# Revit family: QF_BOURGEAT_Self_Meuble_buffet_cuve_froid_statique
name_source: partatom
category: Modèles génériques
revit_build: Autodesk Revit 2015 (Build: 20140606_1530(x64)
units: mm (PartAtom-declared; Revit-internal decimal feet)

## types (12) — shared parameters
Charge max = 200.00 kg
Classe Climatique = 3
Fabricant = BOURGEAT
Fréquence = 50 Hz
Indice de protection = 21
Intensité nominale = 1 A
Nature isolant = mousse polyurethane
Niveau Sonore = 60dBa
Phase = 2
Profondeur hors tout = 1465 mm  [stored 4.80643 ft]
Puissance frigorifique = 272W
Spécification du Fabricant = Meuble buffet cuve froid statique OASIS
Tension = 230 V
Type Fluide Frigorigène = R404a
URL catalogue = http://www.bourgeat.fr

## per-type parameters (varying)
| type | Hauteur hors tout | Longueur hors tout | Modèle | Poids net à vide | Puissance électrique  | lg_barre | lg_meuble_et_cuve | lg_presentoir | pieds | presentoir | roues |
| 5GN-buffet | 900 mm  [stored 2.95276 ft] | 2383 mm  [stored 7.81824 ft] | 853595 | 250.00 kg | 300 W | 1807 mm  [stored 5.92848 ft] | 1851 mm  [stored 6.07283 ft] | 1739 mm  [stored 5.70538 ft] | Oui | Non | Non |
| 5GN-buffet+presentoir_lampe_fluorecente | 1330 mm  [stored 4.36352 ft] | 2383 mm  [stored 7.81824 ft] | 853595+853335 | 277.00 kg | 340 W | 1807 mm  [stored 5.92848 ft] | 1851 mm  [stored 6.07283 ft] | 1739 mm  [stored 5.70538 ft] | Oui | Oui | Non |
| 5GN-buffet+presentoir_lampe_LED | 1330 mm  [stored 4.36352 ft] | 2383 mm  [stored 7.81824 ft] | 853595+853345 | 277.00 kg | 340 W | 1807 mm  [stored 5.92848 ft] | 1851 mm  [stored 6.07283 ft] | 1739 mm  [stored 5.70538 ft] | Oui | Oui | Non |
| 5GN-buffet+roues | 900 mm  [stored 2.95276 ft] | 2383 mm  [stored 7.81824 ft] | 853595+854950 | 250.00 kg | 300 W | 1807 mm  [stored 5.92848 ft] | 1851 mm  [stored 6.07283 ft] | 1739 mm  [stored 5.70538 ft] | Non | Non | Oui |
| 5GN-buffet+presentoir_lampe_fluorecente+roues | 1330 mm  [stored 4.36352 ft] | 2383 mm  [stored 7.81824 ft] | 853595+853335+854950 | 277.00 kg | 340 W | 1807 mm  [stored 5.92848 ft] | 1851 mm  [stored 6.07283 ft] | 1739 mm  [stored 5.70538 ft] | Non | Oui | Oui |
| 5GN-buffet+presentoir_lampe_LED+roues | 1330 mm  [stored 4.36352 ft] | 2383 mm  [stored 7.81824 ft] | 853595+853345+854950 | 277.00 kg | 340 W | 1807 mm  [stored 5.92848 ft] | 1851 mm  [stored 6.07283 ft] | 1739 mm  [stored 5.70538 ft] | Non | Oui | Oui |
| 4GN-buffet | 900 mm  [stored 2.95276 ft] | 2066 mm  [stored 6.77822 ft] | 853594 | 220.00 kg | 300 W | 1490 mm  [stored 4.88845 ft] | 1534 mm  [stored 5.03281 ft] | 1422 mm  [stored 4.66535 ft] | Oui | Non | Non |
| 4GN-buffet+presentoir_lampe_fluorecente | 900 mm  [stored 2.95276 ft] | 2066 mm  [stored 6.77822 ft] | 853594+853334 | 242.00 kg | 332 W | 1490 mm  [stored 4.88845 ft] | 1534 mm  [stored 5.03281 ft] | 1422 mm  [stored 4.66535 ft] | Oui | Oui | Non |
| 4GN-buffet+presentoir_lampe_LED | 900 mm  [stored 2.95276 ft] | 2066 mm  [stored 6.77822 ft] | 853594+853344 | 242.00 kg | 332 W | 1490 mm  [stored 4.88845 ft] | 1534 mm  [stored 5.03281 ft] | 1422 mm  [stored 4.66535 ft] | Oui | Oui | Non |
| 4GN-buffet+roues | 900 mm  [stored 2.95276 ft] | 2066 mm  [stored 6.77822 ft] | 853594+854950 | 220.00 kg | 300 W | 1490 mm  [stored 4.88845 ft] | 1534 mm  [stored 5.03281 ft] | 1422 mm  [stored 4.66535 ft] | Non | Non | Oui |
| 4GN-buffet+presentoir_lampe_fluorecente+roues | 900 mm  [stored 2.95276 ft] | 2066 mm  [stored 6.77822 ft] | 853594+853334+854950 | 242.00 kg | 332 W | 1490 mm  [stored 4.88845 ft] | 1534 mm  [stored 5.03281 ft] | 1422 mm  [stored 4.66535 ft] | Oui | Oui | Non |
| 4GN-buffet+presentoir_lampe_LED+roues | 900 mm  [stored 2.95276 ft] | 2066 mm  [stored 6.77822 ft] | 853594+853344+854950 | 242.00 kg | 332 W | 1490 mm  [stored 4.88845 ft] | 1534 mm  [stored 5.03281 ft] | 1422 mm  [stored 4.66535 ft] | Non | Oui | Oui |

note: [stored X ft] marks values corroborated as IEEE doubles in the binary element streams (Revit-internal decimal feet)

## geometry (parser evidence)
native form markers: Blend x12
no freeform markers — native parametric forms only
